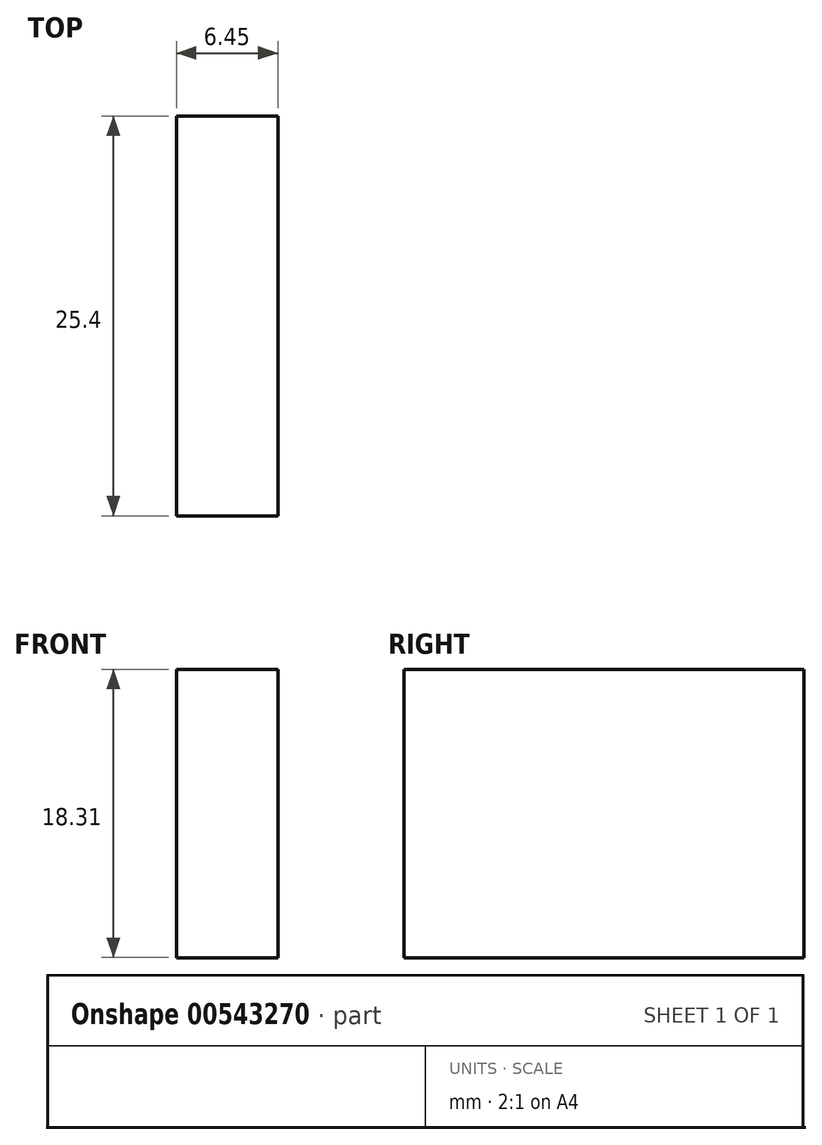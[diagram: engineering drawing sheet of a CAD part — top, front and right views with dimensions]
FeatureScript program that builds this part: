
annotation { "Feature Type Name" : "Feature", "Feature Type Description" : "" }
export const myFeature = defineFeature(function(context is Context, id is Id, definition is map)
    precondition{}
    {
        {
            var Q0;
            Q0=qCreatedBy(makeId("Front.planeOp"),FACE);
            var sketch = newSketch(context, id + "F0", { "sketchPlane" : qUnion([Q0])});
            skLineSegment(sketch, "E0.bottom", {"start": v(-47.43, 64.5) * mm, "end": v(-40.98, 64.5) * mm});
            skLineSegment(sketch, "E0.top", {"start": v(-47.43, 46.19) * mm, "end": v(-40.98, 46.19) * mm});
            skLineSegment(sketch, "E0.left", {"start": v(-47.43, 64.5) * mm, "end": v(-47.43, 46.19) * mm});
            skLineSegment(sketch, "E0.right", {"start": v(-40.98, 64.5) * mm, "end": v(-40.98, 46.19) * mm});
            skSolve(sketch);
        }
        {
            var Q0;
            Q0=makeQuery(id+"F0.imprint","IMPRINT",FACE,{"disambiguationData":[TD([[makeQuery(id+"F0.imprint","IMPRINT",EDGE,{"derivedFrom":sQuery(id+"F0.wireOp",EDGE,"E0.bottom")}),-1.0]])]});
            extrude(context, id + "F1", {"entities" : qUnion([Q0]), "depth" : 25.4 * mm, "offsetDistance" : 25.4 * mm});
        }
    });
